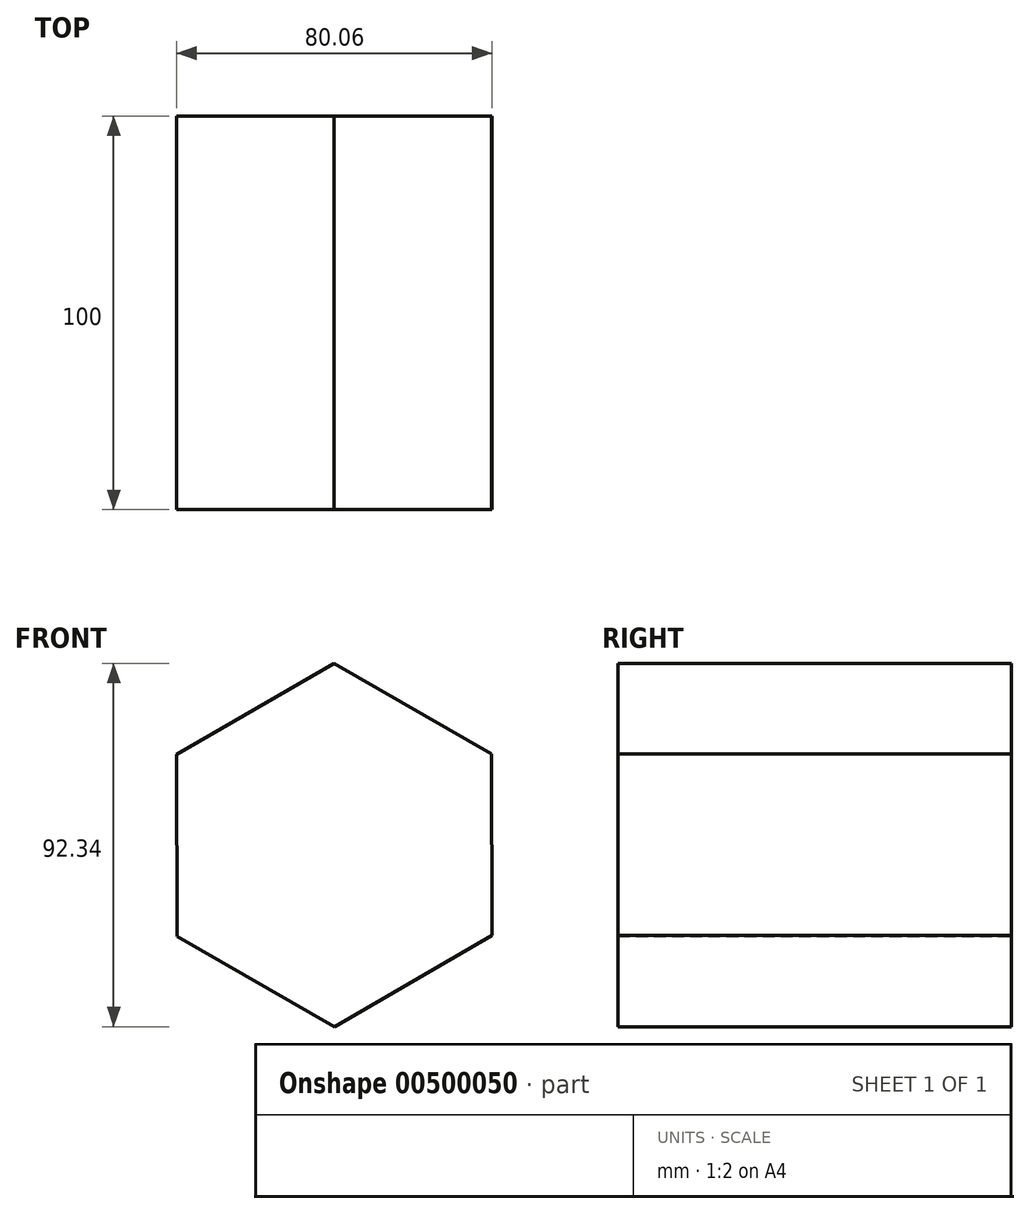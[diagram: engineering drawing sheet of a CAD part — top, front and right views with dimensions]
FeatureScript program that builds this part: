
annotation { "Feature Type Name" : "Feature", "Feature Type Description" : "" }
export const myFeature = defineFeature(function(context is Context, id is Id, definition is map)
    precondition{}
    {
        {
            var Q0;
            Q0=qCreatedBy(makeId("Front.planeOp"),FACE);
            var sketch = newSketch(context, id + "F0", { "sketchPlane" : qUnion([Q0])});
            skCircle(sketch, "E0.cCircle", {"center": v(0, 0) * mm, "radius": 46.17 * mm, "construction": true});
            skLineSegment(sketch, "E0.0", {"start": v(39.93, 23.17) * mm, "end": v(40.03, -23) * mm});
            skLineSegment(sketch, "E0.1", {"start": v(40.03, -23) * mm, "end": v(0.1, -46.17) * mm});
            skLineSegment(sketch, "E0.2", {"start": v(0.1, -46.17) * mm, "end": v(-39.93, -23.17) * mm});
            skLineSegment(sketch, "E0.3", {"start": v(-39.93, -23.17) * mm, "end": v(-40.03, 23) * mm});
            skLineSegment(sketch, "E0.4", {"start": v(-40.03, 23) * mm, "end": v(-0.1, 46.17) * mm});
            skLineSegment(sketch, "E0.5", {"start": v(-0.1, 46.17) * mm, "end": v(39.93, 23.17) * mm});
            skSolve(sketch);
        }
        {
            var Q0;
            Q0 = qSketchRegion(id + "F0", true);
            extrude(context, id + "F1", {"entities" : qUnion([Q0]), "endBound" : BoundingType.SYMMETRIC, "depth" : 100 * mm});
        }
    });
